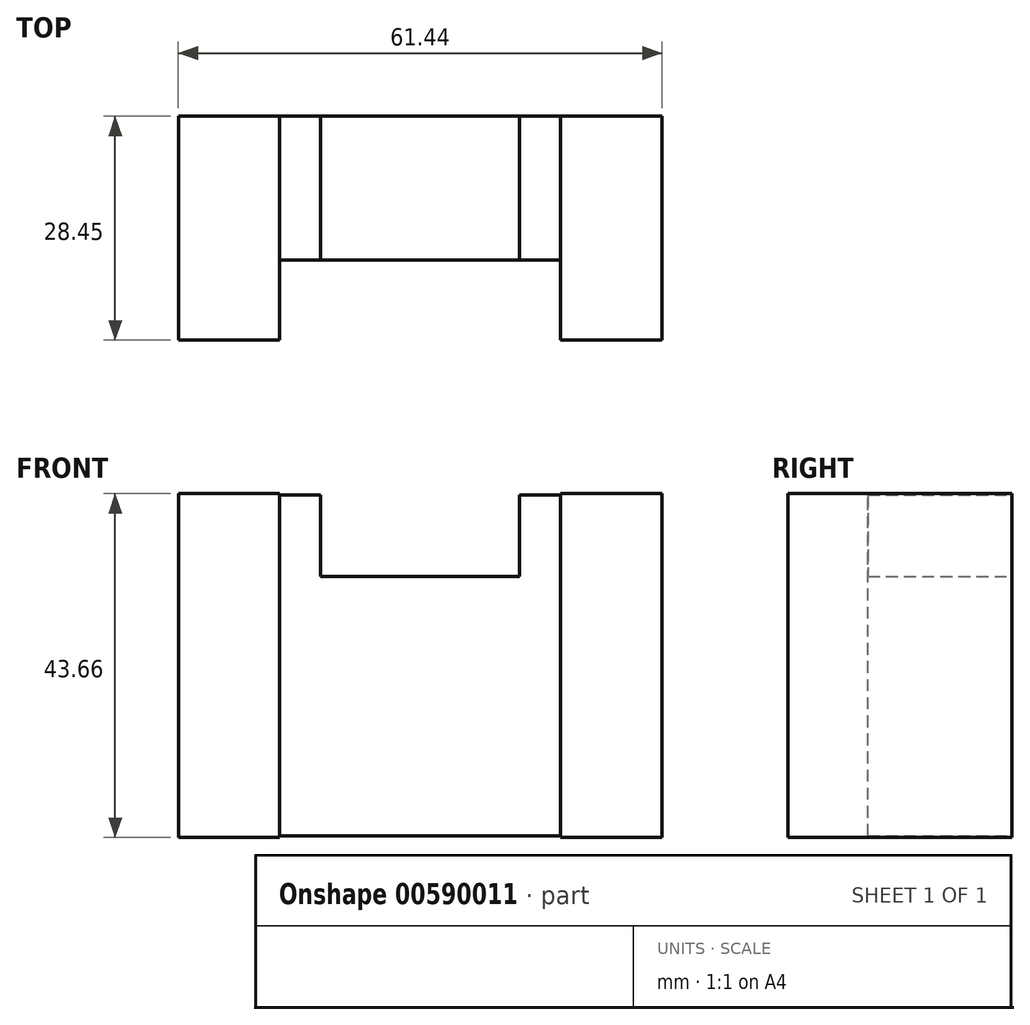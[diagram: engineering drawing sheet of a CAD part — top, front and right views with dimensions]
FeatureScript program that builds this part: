
annotation { "Feature Type Name" : "Feature", "Feature Type Description" : "" }
export const myFeature = defineFeature(function(context is Context, id is Id, definition is map)
    precondition{}
    {
        {
            var Q0;
            Q0=qCreatedBy(makeId("Front.planeOp"),FACE);
            var sketch = newSketch(context, id + "F0", { "sketchPlane" : qUnion([Q0])});
            skLineSegment(sketch, "E0", {"start": v(0, 0) * mm, "end": v(0, -21.64) * mm});
            skLineSegment(sketch, "E1", {"start": v(0, -21.64) * mm, "end": v(-17.84, -21.64) * mm});
            skLineSegment(sketch, "E2.MirrorCS", {"start": v(0, -21.64) * mm, "end": v(17.84, -21.64) * mm});
            skLineSegment(sketch, "E3.MirrorCS", {"start": v(-12.65, 21.64) * mm, "end": v(-17.84, 21.64) * mm});
            skLineSegment(sketch, "E4.MirrorCS", {"start": v(12.65, 21.64) * mm, "end": v(17.84, 21.64) * mm});
            skPoint(sketch, "E5.MirrorCS.end.orphan", {"position": v(0, 21.64) * mm});
            skPoint(sketch, "E5.MirrorCS.start.orphan", {"position": v(0, 0) * mm});
            skLineSegment(sketch, "E6", {"start": v(12.65, 21.64) * mm, "end": v(12.65, 11.28) * mm});
            skLineSegment(sketch, "E7.MirrorCS", {"start": v(-12.65, 21.64) * mm, "end": v(-12.65, 11.28) * mm});
            skLineSegment(sketch, "E8", {"start": v(-12.65, 11.28) * mm, "end": v(12.65, 11.28) * mm});
            skLineSegment(sketch, "E9", {"start": v(-17.84, -21.64) * mm, "end": v(-17.84, 21.64) * mm});
            skLineSegment(sketch, "E10.MirrorCS", {"start": v(17.84, -21.64) * mm, "end": v(17.84, 21.64) * mm});
            skPoint(sketch, "E11.start.orphan", {"position": v(-30.63, 21.64) * mm});
            skPoint(sketch, "E12.orphan", {"position": v(-30.63, -21.64) * mm});
            skPoint(sketch, "E13.end.orphan", {"position": v(30.63, -21.64) * mm});
            skPoint(sketch, "E14.orphan", {"position": v(30.63, 21.64) * mm});
            skSolve(sketch);
        }
        {
            var Q0;
            Q0=makeQuery(id+"F0.imprint","IMPRINT",FACE,{"disambiguationData":[TD([[makeQuery(id+"F0.imprint","IMPRINT",EDGE,{"derivedFrom":sQuery(id+"F0.wireOp",EDGE,"E2.MirrorCS")}),1.0]])]});
            extrude(context, id + "F1", {"entities" : qUnion([Q0]), "depth" : 18.29 * mm, "offsetDistance" : 25.4 * mm});
        }
        {
            var Q0;
            Q0=qCreatedBy(makeId("Front.planeOp"),FACE);
            var sketch = newSketch(context, id + "F2", { "sketchPlane" : qUnion([Q0])});
            skLineSegment(sketch, "E15", {"start": v(-17.84, 21.83) * mm, "end": v(-30.72, 21.83) * mm});
            skLineSegment(sketch, "E16.MirrorCS", {"start": v(-17.84, -21.83) * mm, "end": v(-30.72, -21.83) * mm});
            skLineSegment(sketch, "E17.MirrorCS", {"start": v(17.84, 21.83) * mm, "end": v(30.72, 21.83) * mm});
            skLineSegment(sketch, "E18.MirrorCS", {"start": v(17.84, -21.83) * mm, "end": v(30.72, -21.83) * mm});
            skLineSegment(sketch, "E19", {"start": v(-17.84, 21.83) * mm, "end": v(-17.84, -21.83) * mm});
            skLineSegment(sketch, "E20", {"start": v(-30.72, 21.83) * mm, "end": v(-30.72, -21.83) * mm});
            skLineSegment(sketch, "E21.MirrorCS", {"start": v(17.84, 21.83) * mm, "end": v(17.84, -21.83) * mm});
            skLineSegment(sketch, "E22.MirrorCS", {"start": v(30.72, 21.83) * mm, "end": v(30.72, -21.83) * mm});
            skSolve(sketch);
        }
        {
            var Q0;
            Q0=makeQuery(id+"F2.imprint","IMPRINT",FACE,{"disambiguationData":[TD([[makeQuery(id+"F2.imprint","IMPRINT",EDGE,{"derivedFrom":sQuery(id+"F2.wireOp",EDGE,"E15")}),1.0]])]});
            var Q1;
            Q1=makeQuery(id+"F2.imprint","IMPRINT",FACE,{"disambiguationData":[TD([[makeQuery(id+"F2.imprint","IMPRINT",EDGE,{"derivedFrom":sQuery(id+"F2.wireOp",EDGE,"E17.MirrorCS")}),-1.0]])]});
            extrude(context, id + "F3", {"entities" : qUnion([Q0, Q1]), "depth" : 28.45 * mm, "offsetDistance" : 25.4 * mm});
        }
    });
